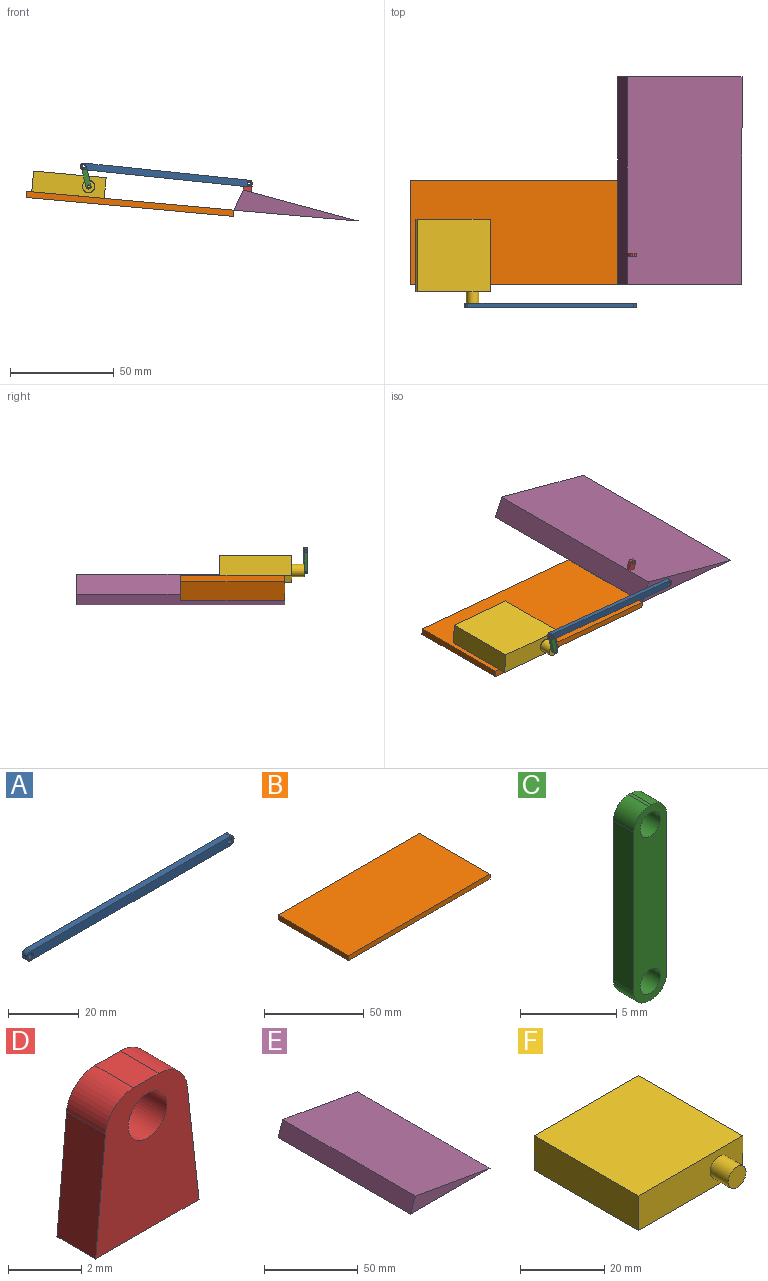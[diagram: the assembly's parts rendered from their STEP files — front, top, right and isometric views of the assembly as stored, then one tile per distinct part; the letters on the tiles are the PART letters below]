
ASSEMBLY  parts=6 mates=6
PART A: 12 faces, bbox 83x2x3.2 mm
  f0: plane 2x0.2mm, normal (-1,0,0), area 0.4mm2, adj f1,f9,f10,f11
  f1: cylinder r=1.5mm len=2mm, axis (0,1,0), area 4.7mm2, adj f0,f2,f10,f11
  f2: plane 80x2mm, normal (0,0,-1), area 160mm2, adj f1,f3,f10,f11
  f3: cylinder r=1.5mm len=2mm, axis (0,1,0), area 4.7mm2, adj f2,f4,f10,f11
  f4: plane 2x0.2mm, normal (1,0,0), area 0.4mm2, adj f3,f5,f10,f11
  f5: cylinder r=1.5mm len=2mm, axis (0,1,0), area 4.7mm2, adj f4,f6,f10,f11
  f6: plane 80x2mm, normal (0,0,1), area 160mm2, adj f5,f9,f10,f11
  f7: cylinder r=1mm len=2mm, axis (0,1,0), area 12.6mm2, adj f10,f11
  f8: cylinder r=1mm len=2mm, axis (0,1,0), area 12.6mm2, adj f10,f11
  f9: cylinder r=1.5mm len=2mm, axis (0,1,0), area 4.7mm2, adj f0,f6,f10,f11
  f10: plane 83x3.2mm, normal (0,-1,0), area 257.4mm2, adj f0,f1,f2,f3,f4,f5,f6,f7
  f11: plane 83x3.2mm, normal (0,1,0), area 257.4mm2, adj f0,f1,f2,f3,f4,f5,f6,f7
PART B: 6 faces, bbox 100x50x3 mm
  f0: plane 100x3mm, normal (0,1,0), area 300mm2, adj f1,f3,f4,f5
  f1: plane 50x3mm, normal (-1,0,0), area 150mm2, adj f0,f2,f4,f5
  f2: plane 100x3mm, normal (0,-1,0), area 300mm2, adj f1,f3,f4,f5
  f3: plane 50x3mm, normal (1,0,0), area 150mm2, adj f0,f2,f4,f5
  f4: plane 100x50mm, normal (0,0,-1), area 5000mm2, adj f0,f1,f2,f3
  f5: plane 100x50mm, normal (0,0,1), area 5000mm2, adj f0,f1,f2,f3
PART C: 12 faces, bbox 2.4x1.5x12.4 mm
  f0: plane 10.2x1.5mm, normal (1,0,0), area 15.3mm2, adj f1,f9,f10,f11
  f1: cylinder r=1.1mm len=1.5mm, axis (0,1,0), area 2.6mm2, adj f0,f2,f10,f11
  f2: plane 1.5x0.2mm, normal (0,0,1), area 0.3mm2, adj f1,f3,f10,f11
  f3: cylinder r=1.1mm len=1.5mm, axis (0,1,0), area 2.6mm2, adj f2,f4,f10,f11
  f4: plane 10.2x1.5mm, normal (-1,0,0), area 15.3mm2, adj f3,f5,f10,f11
  f5: cylinder r=1.1mm len=1.5mm, axis (0,1,0), area 2.6mm2, adj f4,f6,f10,f11
  f6: plane 1.5x0.2mm, normal (0,0,-1), area 0.3mm2, adj f5,f9,f10,f11
  f7: cylinder r=0.75mm len=1.5mm, axis (0,1,0), area 7.1mm2, adj f10,f11
  f8: cylinder r=0.75mm len=1.5mm, axis (0,1,0), area 7.1mm2, adj f10,f11
  f9: cylinder r=1.1mm len=1.5mm, axis (0,1,0), area 2.6mm2, adj f0,f6,f10,f11
  f10: plane 12.4x2.4mm, normal (0,-1,0), area 25.2mm2, adj f0,f1,f2,f3,f4,f5,f6,f7
  f11: plane 12.4x2.4mm, normal (0,1,0), area 25.2mm2, adj f0,f1,f2,f3,f4,f5,f6,f7
PART D: 9 faces, bbox 4x1.5x5 mm
  f0: cylinder r=1.1mm len=1.5mm, axis (0,1,0), area 2.4mm2, adj f1,f6,f7,f8
  f1: plane 4x1.5mm, normal (-1,0,0.09), area 6mm2, adj f0,f2,f7,f8
  f2: plane 4x1.5mm, normal (0,0,-1), area 6mm2, adj f1,f3,f7,f8
  f3: plane 4.02x1.5mm, normal (0.99,0,0.11), area 6.1mm2, adj f2,f4,f7,f8
  f4: cylinder r=1.1mm len=1.5mm, axis (0,1,0), area 2.4mm2, adj f3,f6,f7,f8
  f5: cylinder r=0.75mm len=1.5mm, axis (0,1,0), area 7.1mm2, adj f7,f8
  f6: plane 1.5x0.98mm, normal (0,0,1), area 1.5mm2, adj f0,f4,f7,f8
  f7: plane 5x4mm, normal (0,-1,0), area 15.2mm2, adj f0,f1,f2,f3,f4,f5,f6
  f8: plane 5x4mm, normal (0,1,0), area 15.2mm2, adj f0,f1,f2,f3,f4,f5,f6
PART E: 5 faces, bbox 60x100x10 mm
  f0: plane 100x10mm, normal (-0.94,0,0.34), area 1064.2mm2, adj f1,f2,f3,f4
  f1: plane 100x60mm, normal (0,0,-1), area 6000mm2, adj f0,f2,f3,f4
  f2: plane 100x56.36mm, normal (0.17,0,0.98), area 5724.1mm2, adj f0,f1,f3,f4
  f3: plane 60x10mm, normal (0,1,0), area 300mm2, adj f0,f1,f2
  f4: plane 60x10mm, normal (0,-1,0), area 300mm2, adj f0,f1,f2
PART F: 8 faces, bbox 35x41x10 mm
  f0: plane 35x35mm, normal (0,0,1), area 1225mm2, adj f1,f3,f4,f5
  f1: plane 35x10mm, normal (-1,0,0), area 350mm2, adj f0,f2,f4,f5
  f2: plane 35x35mm, normal (0,0,-1), area 1225mm2, adj f1,f3,f4,f5
  f3: plane 35x10mm, normal (1,0,0), area 350mm2, adj f0,f2,f4,f5
  f4: plane 35x10mm, normal (0,1,0), area 350mm2, adj f0,f1,f2,f3
  f5: plane 35x10mm, normal (0,-1,0), area 321.7mm2, adj f0,f1,f2,f3,f6
  f6: cylinder r=3mm len=6mm, axis (0,1,0), area 113.1mm2, adj f5,f7
  f7: plane 6x6mm, normal (0,-1,0), area 28.3mm2, adj f6
PLACE A rot(axis=(0,1,0),5.9deg) t=(13.79,-13.89,28.05)mm
PLACE B rot(axis=(0,1,0),5.2deg) t=(-3.64,20.11,15.65)mm fixed
PLACE C rot(axis=(0,-1,0),14deg) t=(-24.79,-14.39,27.33)mm
PLACE D rot(axis=(0,1,0),15deg) t=(52.58,10.16,20.24)mm
PLACE E rot(axis=(0,1,0),5deg) t=(46.16,-4.89,11.11)mm
PLACE F rot(axis=(0,1,0),5.2deg) t=(-23.59,-8.39,22.48)mm
MATE fastened F.f2 <-> B.f5  axis (-0.09,0,-1) through (-33.51,30.11,18.37)mm
MATE revolute A.f7 <-> C.f7  axis (0,-1,0) through (-26,-15.89,32.19)mm
MATE cylindrical A.f8 <-> D.f5  axis (0,1,0) through (53.57,-13.89,23.91)mm
MATE revolute E.f4 <-> B.f2  axis (0,-1,0) through (46.16,-4.89,11.11)mm
MATE fastened D.f2 <-> E.f2  axis (-0.26,0,-0.97) through (52.58,9.41,20.24)mm
MATE revolute C.f8 <-> F.f6  axis (0,1,0) through (-23.59,-14.39,22.48)mm
